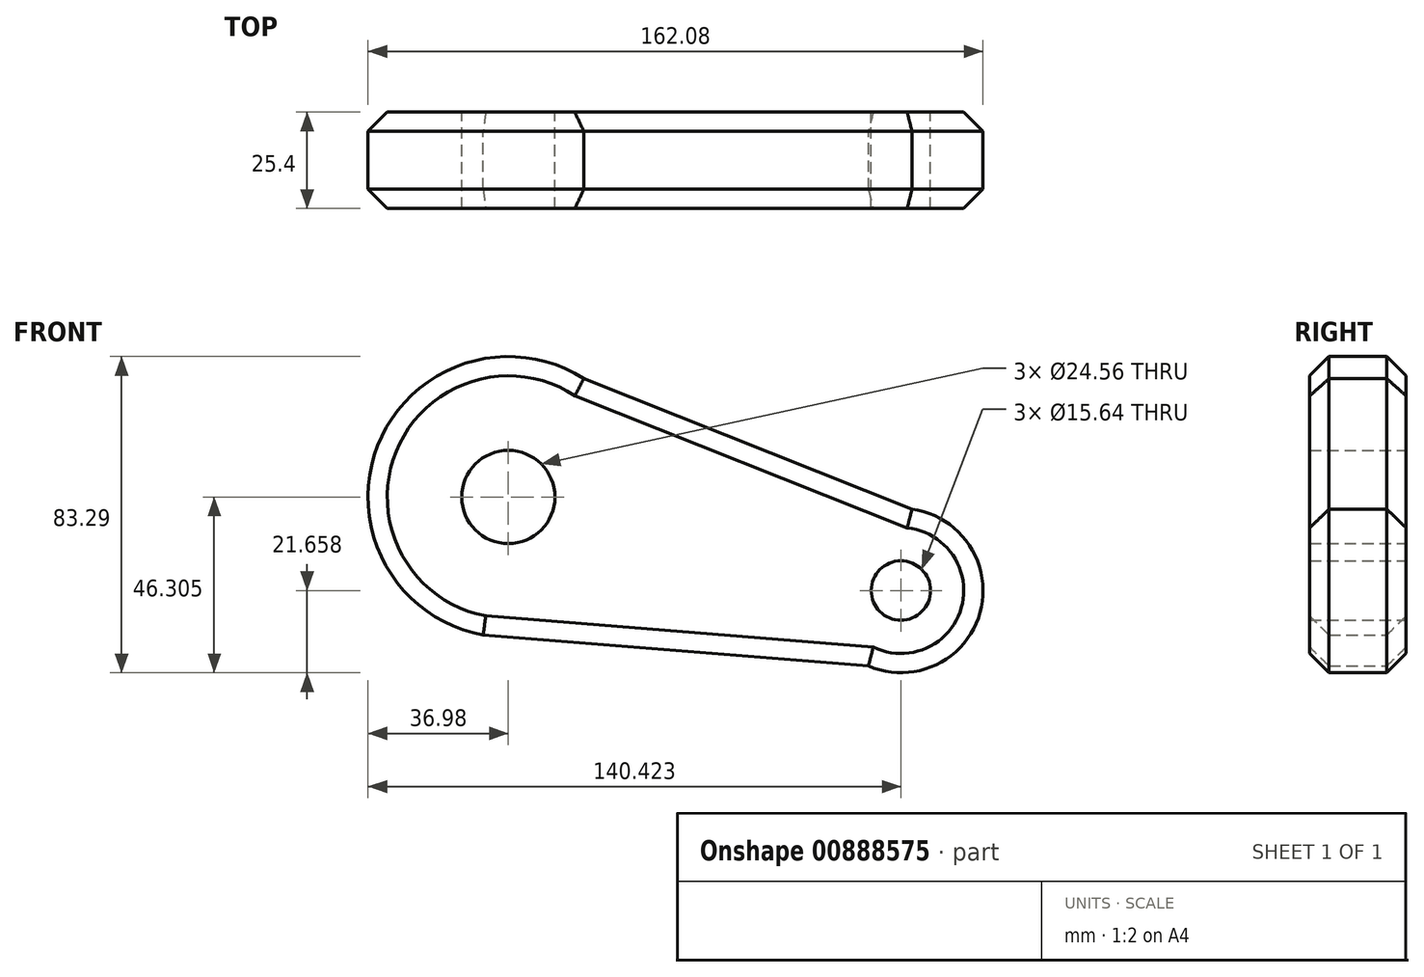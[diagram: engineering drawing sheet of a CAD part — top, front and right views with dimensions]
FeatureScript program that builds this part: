
annotation { "Feature Type Name" : "Feature", "Feature Type Description" : "" }
export const myFeature = defineFeature(function(context is Context, id is Id, definition is map)
    precondition{}
    {
        {
            var Q0;
            Q0=qCreatedBy(makeId("Front.planeOp"),FACE);
            var sketch = newSketch(context, id + "F0", { "sketchPlane" : qUnion([Q0])});
            skCircle(sketch, "E0", {"center": v(33.14, 15.5) * mm, "radius": 21.65 * mm});
            skCircle(sketch, "E1", {"center": v(-70.3, 40.15) * mm, "radius": 36.98 * mm});
            skLineSegment(sketch, "E2", {"start": v(-50.42, 71.33) * mm, "end": v(36.08, 36.95) * mm});
            skLineSegment(sketch, "E3", {"start": v(-76.91, 3.76) * mm, "end": v(24.59, -4.4) * mm});
            skCircle(sketch, "E4", {"center": v(-70.3, 40.15) * mm, "radius": 12.28 * mm});
            skCircle(sketch, "E5", {"center": v(33.14, 15.5) * mm, "radius": 7.82 * mm});
            skSolve(sketch);
        }
        {
            var Q0;
            Q0=makeQuery(id+"F0.imprint","IMPRINT",FACE,{"disambiguationData":[TD([[makeQuery(id+"F0.imprint","IMPRINT",EDGE,{"derivedFrom":sQuery(id+"F0.wireOp",EDGE,"E4")}),-1.0]])]});
            var Q1;
            Q1=makeQuery(id+"F0.imprint","IMPRINT",FACE,{"disambiguationData":[TD([[makeQuery(id+"F0.imprint","IMPRINT",EDGE,{"derivedFrom":sQuery(id+"F0.wireOp",EDGE,"E5")}),-1.0]])]});
            var Q2;
            {var subQ0=sQuery(id+"F0.wireOp",EDGE,"E2");Q2=makeQuery(id+"F0.imprint","IMPRINT",FACE,{"disambiguationData":[TD([[makeQuery(id+"F0.imprint","IMPRINT",EDGE,{"derivedFrom":subQ0}),-1.0]])]});}
            extrude(context, id + "F1", {"entities" : qUnion([Q0, Q1, Q2]), "depth" : 25.4 * mm, "offsetDistance" : 25.4 * mm});
        }
        {
            var Q0;
            Q0=makeQuery(id+"F1.opExtrude","CAP_EDGE",EDGE,{"disambiguationData":[OSD([sQuery(id+"F0.wireOp",EDGE,"E2")])],"isStart":false});
            var Q1;
            Q1=makeQuery(id+"F1.opExtrude","CAP_EDGE",EDGE,{"disambiguationData":[OSD([sQuery(id+"F0.wireOp",EDGE,"E0")])],"isStart":false});
            var Q2;
            Q2=makeQuery(id+"F1.opExtrude","CAP_EDGE",EDGE,{"disambiguationData":[OSD([sQuery(id+"F0.wireOp",EDGE,"E3")])],"isStart":false});
            var Q3;
            Q3=makeQuery(id+"F1.opExtrude","CAP_EDGE",EDGE,{"disambiguationData":[OSD([sQuery(id+"F0.wireOp",EDGE,"E1")])],"isStart":false});
            var Q4;
            Q4=makeQuery(id+"F1.opExtrude","CAP_EDGE",EDGE,{"disambiguationData":[OSD([sQuery(id+"F0.wireOp",EDGE,"E2")])],"isStart":true});
            var Q5;
            Q5=makeQuery(id+"F1.opExtrude","CAP_EDGE",EDGE,{"disambiguationData":[OSD([sQuery(id+"F0.wireOp",EDGE,"E0")])],"isStart":true});
            var Q6;
            Q6=makeQuery(id+"F1.opExtrude","CAP_EDGE",EDGE,{"disambiguationData":[OSD([sQuery(id+"F0.wireOp",EDGE,"E3")])],"isStart":true});
            var Q7;
            Q7=makeQuery(id+"F1.opExtrude","CAP_EDGE",EDGE,{"disambiguationData":[OSD([sQuery(id+"F0.wireOp",EDGE,"E1")])],"isStart":true});
            chamfer(context, id + "F2", {"entities" : qUnion([Q0, Q1, Q2, Q3, Q4, Q5, Q6, Q7]), "width" : 5.08 * mm, "tangentPropagation" : true});
        }
    });
